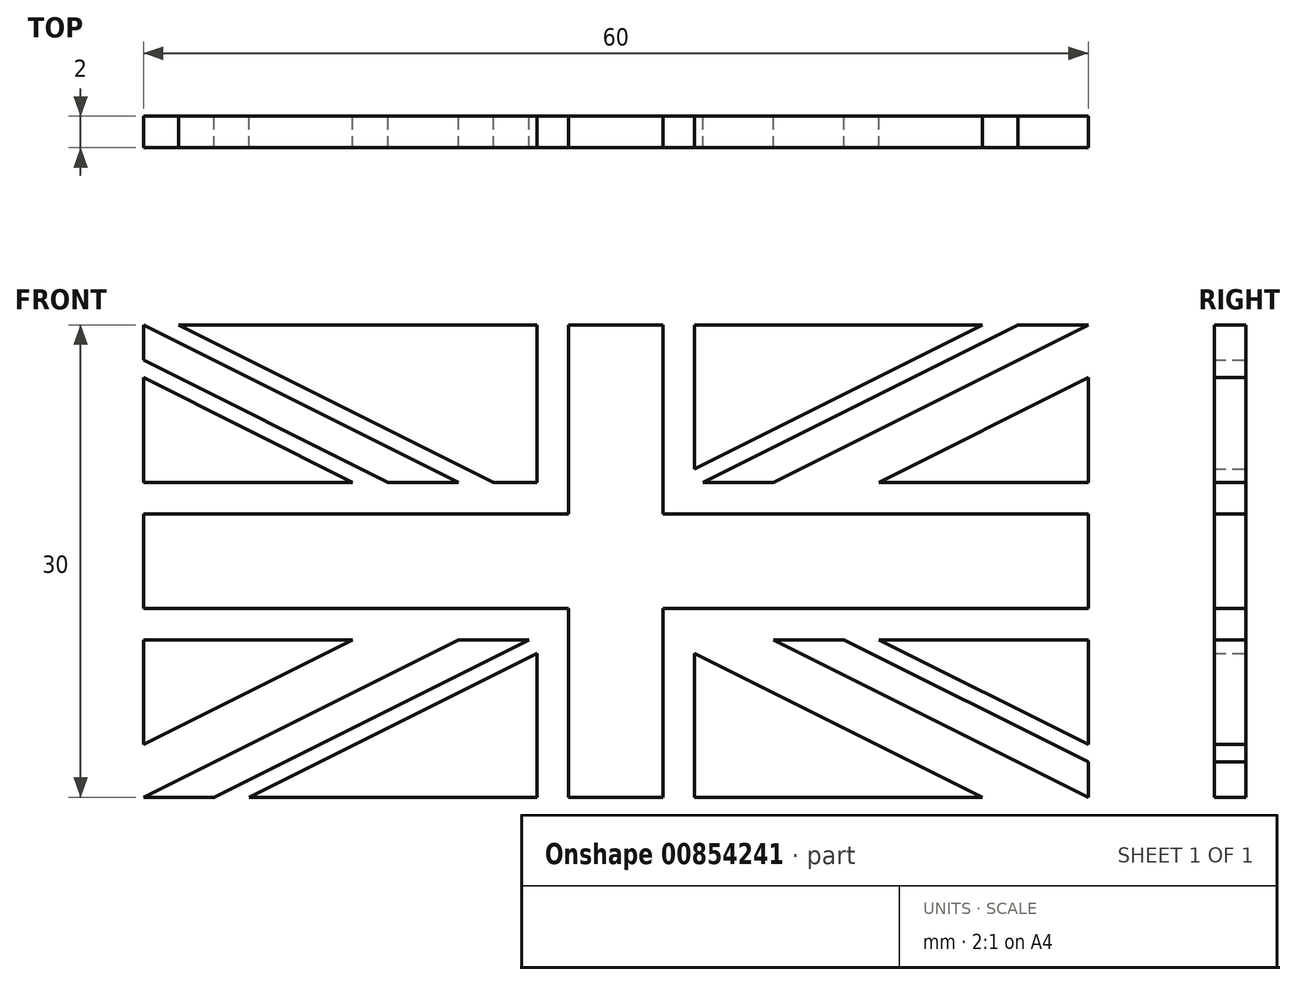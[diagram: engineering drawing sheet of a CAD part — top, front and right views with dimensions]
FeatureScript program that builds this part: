
annotation { "Feature Type Name" : "Feature", "Feature Type Description" : "" }
export const myFeature = defineFeature(function(context is Context, id is Id, definition is map)
    precondition{}
    {
        {
            var Q0;
            Q0=qCreatedBy(makeId("Front.planeOp"),FACE);
            var sketch = newSketch(context, id + "F0", { "sketchPlane" : qUnion([Q0])});
            skLineSegment(sketch, "E0.bottom", {"start": v(-30, -15) * mm, "end": v(-25.53, -15) * mm});
            skLineSegment(sketch, "E0.top", {"start": v(-27.76, 15) * mm, "end": v(-5, 15) * mm});
            skPoint(sketch, "E0.middle", {"position": v(0, 0) * mm});
            skLineSegment(sketch, "E1.bottom", {"start": v(-23.3, -15) * mm, "end": v(-5, -15) * mm});
            skLineSegment(sketch, "E1.top", {"start": v(-30, -5) * mm, "end": v(-16.7, -5) * mm});
            skLineSegment(sketch, "E1.left", {"start": v(-30, -11.65) * mm, "end": v(-30, -5) * mm});
            skLineSegment(sketch, "E1.right", {"start": v(-5, -15) * mm, "end": v(-5, -5.85) * mm});
            skLineSegment(sketch, "E2.top", {"start": v(-30, 5) * mm, "end": v(-16.7, 5) * mm});
            skLineSegment(sketch, "E2.left", {"start": v(-30, 15) * mm, "end": v(-30, 12.76) * mm});
            skLineSegment(sketch, "E2.right", {"start": v(-5, 15) * mm, "end": v(-5, 5) * mm});
            skLineSegment(sketch, "E3.bottom", {"start": v(30, 15) * mm, "end": v(25.53, 15) * mm});
            skLineSegment(sketch, "E3.top", {"start": v(30, 5) * mm, "end": v(16.7, 5) * mm});
            skLineSegment(sketch, "E3.left", {"start": v(30, 11.65) * mm, "end": v(30, 5) * mm});
            skLineSegment(sketch, "E3.right", {"start": v(5, 15) * mm, "end": v(5, 5.85) * mm});
            skLineSegment(sketch, "E4.left", {"start": v(30, -15) * mm, "end": v(30, -12.76) * mm});
            skLineSegment(sketch, "E5.bottom", {"start": v(30, -3) * mm, "end": v(3, -3) * mm});
            skLineSegment(sketch, "E5.top", {"start": v(30, 3) * mm, "end": v(3, 3) * mm});
            skLineSegment(sketch, "E5.left", {"start": v(30, -3) * mm, "end": v(30, 3) * mm});
            skLineSegment(sketch, "E5.right", {"start": v(-30, -3) * mm, "end": v(-30, 3) * mm});
            skLineSegment(sketch, "E6.bottom", {"start": v(3, -15) * mm, "end": v(-3, -15) * mm});
            skLineSegment(sketch, "E6.top", {"start": v(3, 15) * mm, "end": v(-3, 15) * mm});
            skLineSegment(sketch, "E6.left", {"start": v(3, -15) * mm, "end": v(3, -3) * mm});
            skLineSegment(sketch, "E6.right", {"start": v(-3, -15) * mm, "end": v(-3, -3) * mm});
            skLineSegment(sketch, "E7.trimOffspring", {"start": v(-3, -15) * mm, "end": v(3, -15) * mm});
            skLineSegment(sketch, "E8.trimOffspring", {"start": v(5, -15) * mm, "end": v(23.3, -15) * mm});
            skLineSegment(sketch, "E9.trimOffspring", {"start": v(-3, -3) * mm, "end": v(-30, -3) * mm});
            skLineSegment(sketch, "E10.trimOffspring", {"start": v(-3, 3) * mm, "end": v(-30, 3) * mm});
            skLineSegment(sketch, "E11.trimOffspring", {"start": v(-3, 3) * mm, "end": v(-3, 15) * mm});
            skLineSegment(sketch, "E12.trimOffspring", {"start": v(3, 3) * mm, "end": v(3, 15) * mm});
            skLineSegment(sketch, "E13.trimOffspring", {"start": v(30, 5) * mm, "end": v(30, 11.65) * mm});
            skLineSegment(sketch, "E14.trimOffspring", {"start": v(5, 15) * mm, "end": v(23.3, 15) * mm});
            skLineSegment(sketch, "E15.trimOffspring", {"start": v(-3, 15) * mm, "end": v(3, 15) * mm});
            skLineSegment(sketch, "E16.trimOffspring", {"start": v(-30, 5) * mm, "end": v(-30, 11.65) * mm});
            skLineSegment(sketch, "E17", {"start": v(30, 15) * mm, "end": v(10, 5) * mm});
            skLineSegment(sketch, "E18.0", {"start": v(-30, 12.76) * mm, "end": v(-14.47, 5) * mm});
            skLineSegment(sketch, "E19.0", {"start": v(-30, 11.65) * mm, "end": v(-16.7, 5) * mm});
            skLineSegment(sketch, "E20.0", {"start": v(30, 11.65) * mm, "end": v(16.7, 5) * mm});
            skLineSegment(sketch, "E21.0", {"start": v(25.53, 15) * mm, "end": v(5.53, 5) * mm});
            skLineSegment(sketch, "E22.trimOffspring", {"start": v(-16.7, -5) * mm, "end": v(-30, -11.65) * mm});
            skLineSegment(sketch, "E23.trimOffspring", {"start": v(-10, -5) * mm, "end": v(-30, -15) * mm});
            skLineSegment(sketch, "E24.trimOffspring", {"start": v(-5.53, -5) * mm, "end": v(-25.53, -15) * mm});
            skLineSegment(sketch, "E25.trimOffspring", {"start": v(-5, -5.85) * mm, "end": v(-23.3, -15) * mm});
            skLineSegment(sketch, "E26.trimOffspring", {"start": v(14.47, -5) * mm, "end": v(30, -12.76) * mm});
            skLineSegment(sketch, "E27.trimOffspring", {"start": v(16.7, -5) * mm, "end": v(30, -11.65) * mm});
            skLineSegment(sketch, "E28.trimOffspring", {"start": v(5, -5.85) * mm, "end": v(23.3, -15) * mm});
            skLineSegment(sketch, "E29.0", {"start": v(23.3, 15) * mm, "end": v(5, 5.85) * mm});
            skLineSegment(sketch, "E30", {"start": v(30, -15) * mm, "end": v(10, -5) * mm});
            skLineSegment(sketch, "E31.trimOffspring", {"start": v(-10, 5) * mm, "end": v(-30, 15) * mm});
            skLineSegment(sketch, "E32.trimOffspring", {"start": v(-7.76, 5) * mm, "end": v(-27.76, 15) * mm});
            skLineSegment(sketch, "E33.trimOffspring", {"start": v(-30, 11.65) * mm, "end": v(-30, 5) * mm});
            skLineSegment(sketch, "E34.trimOffspring", {"start": v(-30, 12.76) * mm, "end": v(-30, 15) * mm});
            skLineSegment(sketch, "E35.trimOffspring", {"start": v(-14.47, 5) * mm, "end": v(-10, 5) * mm});
            skLineSegment(sketch, "E36.trimOffspring", {"start": v(-7.76, 5) * mm, "end": v(-5, 5) * mm});
            skLineSegment(sketch, "E37.trimOffspring", {"start": v(10, 5) * mm, "end": v(5.53, 5) * mm});
            skLineSegment(sketch, "E38.trimOffspring", {"start": v(23.3, 15) * mm, "end": v(5, 15) * mm});
            skLineSegment(sketch, "E39.trimOffspring", {"start": v(25.53, 15) * mm, "end": v(30, 15) * mm});
            skLineSegment(sketch, "E40.trimOffspring", {"start": v(30, -11.65) * mm, "end": v(30, -5) * mm});
            skLineSegment(sketch, "E41", {"start": v(5, -5.85) * mm, "end": v(5, -15) * mm});
            skLineSegment(sketch, "E42", {"start": v(16.7, -5) * mm, "end": v(30, -5) * mm});
            skLineSegment(sketch, "E43", {"start": v(10, -5) * mm, "end": v(14.47, -5) * mm});
            skLineSegment(sketch, "E44.trimOffspring", {"start": v(-10, -5) * mm, "end": v(-5.53, -5) * mm});
            skSolve(sketch);
        }
        {
            var Q0;
            Q0 = qSketchRegion(id + "F0", true);
            var Q1;
            Q1=makeQuery(id+"F0.imprint","IMPRINT",FACE,{"disambiguationData":[TD([[makeQuery(id+"F0.imprint","IMPRINT",EDGE,{"derivedFrom":sQuery(id+"F0.wireOp",EDGE,"E5.bottom")}),-1.0]])]});
            extrude(context, id + "F1", {"entities" : qUnion([Q0, Q1]), "depth" : 2 * mm, "offsetDistance" : 25 * mm});
        }
    });
